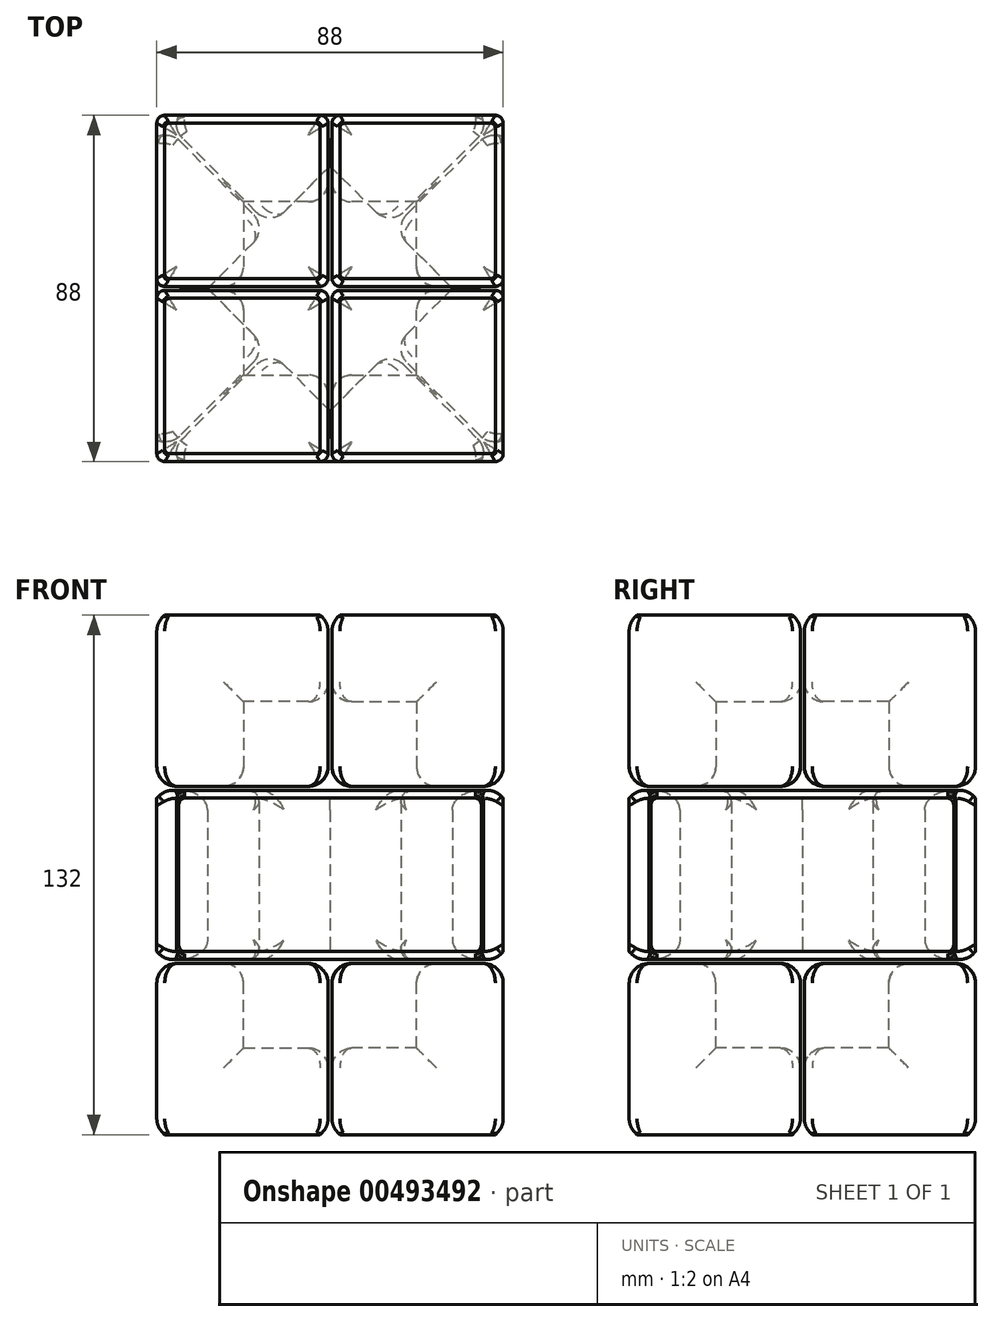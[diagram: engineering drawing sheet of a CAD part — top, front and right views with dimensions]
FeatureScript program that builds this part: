
annotation { "Feature Type Name" : "Feature", "Feature Type Description" : "" }
export const myFeature = defineFeature(function(context is Context, id is Id, definition is map)
    precondition{}
    {
        {
            assignVariable(context, id + "F0", {"name" : "Cubie", "anyValue" : 22});
        }
        {
            assignVariable(context, id + "F1", {"name" : "Tollerance", "anyValue" : 0.5});
        }
        {
            var Q0;
            Q0=qCreatedBy(makeId("Front.planeOp"),FACE);
            var sketch = newSketch(context, id + "F2", { "sketchPlane" : qUnion([Q0])});
            skLineSegment(sketch, "E0", {"start": v(0, 74.98) * mm, "end": v(0, -74.26) * mm, "construction": true});
            skSolve(sketch);
        }
        {
            var Q0;
            Q0=qCreatedBy(makeId("Top.planeOp"),FACE);
            var sketch = newSketch(context, id + "F3", { "sketchPlane" : qUnion([Q0])});
            skLineSegment(sketch, "E1.bottom", {"start": v(22, 22) * mm, "end": v(-22, 22) * mm});
            skLineSegment(sketch, "E1.top", {"start": v(22, -22) * mm, "end": v(-22, -22) * mm});
            skLineSegment(sketch, "E1.left", {"start": v(22, 22) * mm, "end": v(22, -22) * mm});
            skLineSegment(sketch, "E1.right", {"start": v(-22, 22) * mm, "end": v(-22, -22) * mm});
            skPoint(sketch, "E1.middle", {"position": v(0, 0) * mm});
            skLineSegment(sketch, "E2", {"start": v(0, 22) * mm, "end": v(0, -22) * mm});
            skLineSegment(sketch, "E3", {"start": v(-22, 0) * mm, "end": v(22, 0) * mm});
            skLineSegment(sketch, "E4", {"start": v(-31.11, 0) * mm, "end": v(0, 31.11) * mm});
            skLineSegment(sketch, "E5", {"start": v(0, 31.11) * mm, "end": v(31.11, 0) * mm});
            skLineSegment(sketch, "E6", {"start": v(31.11, 0) * mm, "end": v(0, -31.11) * mm});
            skLineSegment(sketch, "E7", {"start": v(0, -31.11) * mm, "end": v(-31.11, 0) * mm});
            skLineSegment(sketch, "E8", {"start": v(-15.56, 15.56) * mm, "end": v(15.56, -15.56) * mm});
            skLineSegment(sketch, "E9", {"start": v(-15.56, -15.56) * mm, "end": v(15.56, 15.56) * mm});
            skLineSegment(sketch, "E10.bottom", {"start": v(44, 44) * mm, "end": v(-44, 44) * mm});
            skLineSegment(sketch, "E10.top", {"start": v(44, -44) * mm, "end": v(-44, -44) * mm});
            skLineSegment(sketch, "E10.left", {"start": v(44, 44) * mm, "end": v(44, -44) * mm});
            skLineSegment(sketch, "E10.right", {"start": v(-44, 44) * mm, "end": v(-44, -44) * mm});
            skLineSegment(sketch, "E11", {"start": v(-44, 44) * mm, "end": v(44, -44) * mm});
            skLineSegment(sketch, "E12", {"start": v(-44, -44) * mm, "end": v(44, 44) * mm});
            skLineSegment(sketch, "E13", {"start": v(-44, 0) * mm, "end": v(44, 0) * mm});
            skLineSegment(sketch, "E14", {"start": v(0, 44) * mm, "end": v(0, -44) * mm});
            skLineSegment(sketch, "E15", {"start": v(-44, 44) * mm, "end": v(-22, 22) * mm});
            skLineSegment(sketch, "E16", {"start": v(22, 22) * mm, "end": v(44, 44) * mm});
            skSolve(sketch);
        }
        {
            var Q0;
            Q0=qCreatedBy(makeId("Top.planeOp"),FACE);
            var sketch = newSketch(context, id + "F4", { "sketchPlane" : qUnion([Q0])});
            skLineSegment(sketch, "E17", {"start": v(-15.2, 15.9) * mm, "end": v(-43.3, 44) * mm});
            skLineSegment(sketch, "E18", {"start": v(-43.3, 44) * mm, "end": v(43.3, 44) * mm});
            skLineSegment(sketch, "E19", {"start": v(43.3, 44) * mm, "end": v(15.2, 15.9) * mm});
            skLineSegment(sketch, "E20", {"start": v(15.2, 15.9) * mm, "end": v(0, 31.11) * mm});
            skLineSegment(sketch, "E21", {"start": v(0, 31.11) * mm, "end": v(-15.2, 15.9) * mm});
            skSolve(sketch);
        }
        {
            var Q0;
            Q0 = qSketchRegion(id + "F4", true);
            extrude(context, id + "F5", {"entities" : qUnion([Q0]), "endBound" : BoundingType.SYMMETRIC, "depth" : (getVariable(context, 'Cubie') * 2 - getVariable(context, 'Tollerance') * 2) * mm});
        }
        {
            var Q0;
            Q0=qCreatedBy(makeId("Top.planeOp"),FACE);
            var sketch = newSketch(context, id + "F6", { "sketchPlane" : qUnion([Q0])});
            skLineSegment(sketch, "E22", {"start": v(-44, 0.5) * mm, "end": v(-44, 44) * mm});
            skLineSegment(sketch, "E23", {"start": v(-44, 44) * mm, "end": v(-0.5, 44) * mm});
            skLineSegment(sketch, "E24", {"start": v(-0.5, 44) * mm, "end": v(-0.5, 22) * mm});
            skLineSegment(sketch, "E25", {"start": v(-0.5, 22) * mm, "end": v(-22, 22) * mm});
            skLineSegment(sketch, "E26", {"start": v(-22, 22) * mm, "end": v(-22, 0.5) * mm});
            skLineSegment(sketch, "E27", {"start": v(-22, 0.5) * mm, "end": v(-44, 0.5) * mm});
            skSolve(sketch);
        }
        {
            var Q0;
            Q0 = qSketchRegion(id + "F6", true);
            extrude(context, id + "F7", {"entities" : qUnion([Q0]), "depth" : (getVariable(context, 'Cubie') - getVariable(context, 'Tollerance')) * mm});
        }
        {
            var Q0;
            Q0=makeQuery(id+"F7.opExtrude","SWEPT_BODY",BODY,{"disambiguationData":[OSD([sQuery(id+"F6.wireOp",EDGE,"E22"),sQuery(id+"F6.wireOp",EDGE,"E23"),sQuery(id+"F6.wireOp",EDGE,"E24"),sQuery(id+"F6.wireOp",EDGE,"E25"),sQuery(id+"F6.wireOp",EDGE,"E26"),sQuery(id+"F6.wireOp",EDGE,"E27")])]});
            transform(context, id + "F8", {"entities" : qUnion([Q0]), "transformType" : TransformType.TRANSLATION_3D, "dx" : 0 * mm, "dy" : 0 * mm, "dz" : (getVariable(context, 'Cubie') + getVariable(context, 'Tollerance')) * mm, "makeCopy" : false});
        }
        {
            var Q0;
            Q0=makeQuery(id+"F7.opExtrude","CAP_FACE",FACE,{"disambiguationData":[OSD([sQuery(id+"F6.wireOp",EDGE,"E22"),sQuery(id+"F6.wireOp",EDGE,"E23"),sQuery(id+"F6.wireOp",EDGE,"E24"),sQuery(id+"F6.wireOp",EDGE,"E25"),sQuery(id+"F6.wireOp",EDGE,"E26"),sQuery(id+"F6.wireOp",EDGE,"E27")])],"isStart":false});
            var sketch = newSketch(context, id + "F9", { "sketchPlane" : qUnion([Q0])});
            skLineSegment(sketch, "E28", {"start": v(-44, 0.5) * mm, "end": v(-44, 44) * mm});
            skLineSegment(sketch, "E29", {"start": v(-44, 44) * mm, "end": v(-0.5, 44) * mm});
            skLineSegment(sketch, "E30", {"start": v(-0.5, 44) * mm, "end": v(-0.5, 0.5) * mm});
            skLineSegment(sketch, "E31", {"start": v(-0.5, 0.5) * mm, "end": v(-44, 0.5) * mm});
            skSolve(sketch);
        }
        {
            var Q0;
            Q0 = qSketchRegion(id + "F9", true);
            extrude(context, id + "F10", {"entities" : qUnion([Q0]), "operationType" : NewBodyOperationType.ADD, "depth" : (getVariable(context, 'Cubie')) * mm});
        }
        {
            var Q0;
            Q0=makeQuery(id+"F10.opExtrude","CAP_FACE",FACE,{"disambiguationData":[OSD([sQuery(id+"F9.wireOp",EDGE,"E28"),sQuery(id+"F9.wireOp",EDGE,"E29"),sQuery(id+"F9.wireOp",EDGE,"E30"),sQuery(id+"F9.wireOp",EDGE,"E31")])],"isStart":false});
            var Q1;
            Q1=makeQuery(id+"F5.opExtrude","SWEPT_FACE",FACE,{"disambiguationData":[OSD([sQuery(id+"F4.wireOp",EDGE,"E18")])]});
            chamfer(context, id + "F11", {"entities" : qUnion([Q0, Q1]), "width" : 2 * mm, "tangentPropagation" : true});
        }
        {
            var Q0;
            {var subQ0=sQuery(id+"F9.wireOp",EDGE,"E29");Q0=makeQuery(id+"F11.opChamfer","BLEND_EDGE",EDGE,{"blendedFrom":[makeQuery(id+"F10.opExtrude","CAP_EDGE",EDGE,{"disambiguationData":[OSD([subQ0])],"isStart":false}),makeQuery(id+"F10.boolean.opBoolean","MERGE",FACE,{"derivedFrom":[makeQuery(id+"F7.opExtrude","SWEPT_FACE",FACE,{"disambiguationData":[OSD([sQuery(id+"F6.wireOp",EDGE,"E23")])]}),makeQuery(id+"F10.opExtrude","SWEPT_FACE",FACE,{"disambiguationData":[OSD([subQ0])]})]})],"blendedInto":[makeQuery(id+"F10.boolean.opBoolean","MERGE",FACE,{"derivedFrom":[makeQuery(id+"F7.opExtrude","SWEPT_FACE",FACE,{"disambiguationData":[OSD([sQuery(id+"F6.wireOp",EDGE,"E23")])]}),makeQuery(id+"F10.opExtrude","SWEPT_FACE",FACE,{"disambiguationData":[OSD([subQ0])]})]})]});}
            var Q1;
            {var subQ0=sQuery(id+"F9.wireOp",EDGE,"E30");Q1=makeQuery(id+"F11.opChamfer","BLEND_EDGE",EDGE,{"blendedFrom":[makeQuery(id+"F10.opExtrude","CAP_EDGE",EDGE,{"disambiguationData":[OSD([subQ0])],"isStart":false}),makeQuery(id+"F10.boolean.opBoolean","MERGE",FACE,{"derivedFrom":[makeQuery(id+"F7.opExtrude","SWEPT_FACE",FACE,{"disambiguationData":[OSD([sQuery(id+"F6.wireOp",EDGE,"E24")])]}),makeQuery(id+"F10.opExtrude","SWEPT_FACE",FACE,{"disambiguationData":[OSD([subQ0])]})]})],"blendedInto":[makeQuery(id+"F10.boolean.opBoolean","MERGE",FACE,{"derivedFrom":[makeQuery(id+"F7.opExtrude","SWEPT_FACE",FACE,{"disambiguationData":[OSD([sQuery(id+"F6.wireOp",EDGE,"E24")])]}),makeQuery(id+"F10.opExtrude","SWEPT_FACE",FACE,{"disambiguationData":[OSD([subQ0])]})]})]});}
            var Q2;
            {var subQ0=sQuery(id+"F9.wireOp",EDGE,"E28");Q2=makeQuery(id+"F11.opChamfer","BLEND_EDGE",EDGE,{"blendedFrom":[makeQuery(id+"F10.opExtrude","CAP_EDGE",EDGE,{"disambiguationData":[OSD([subQ0])],"isStart":false}),makeQuery(id+"F10.boolean.opBoolean","MERGE",FACE,{"derivedFrom":[makeQuery(id+"F7.opExtrude","SWEPT_FACE",FACE,{"disambiguationData":[OSD([sQuery(id+"F6.wireOp",EDGE,"E22")])]}),makeQuery(id+"F10.opExtrude","SWEPT_FACE",FACE,{"disambiguationData":[OSD([subQ0])]})]})],"blendedInto":[makeQuery(id+"F10.boolean.opBoolean","MERGE",FACE,{"derivedFrom":[makeQuery(id+"F7.opExtrude","SWEPT_FACE",FACE,{"disambiguationData":[OSD([sQuery(id+"F6.wireOp",EDGE,"E22")])]}),makeQuery(id+"F10.opExtrude","SWEPT_FACE",FACE,{"disambiguationData":[OSD([subQ0])]})]})]});}
            var Q3;
            {var subQ0=sQuery(id+"F9.wireOp",EDGE,"E31");Q3=makeQuery(id+"F11.opChamfer","BLEND_EDGE",EDGE,{"blendedFrom":[makeQuery(id+"F10.opExtrude","CAP_EDGE",EDGE,{"disambiguationData":[OSD([subQ0])],"isStart":false}),makeQuery(id+"F10.boolean.opBoolean","MERGE",FACE,{"derivedFrom":[makeQuery(id+"F7.opExtrude","SWEPT_FACE",FACE,{"disambiguationData":[OSD([sQuery(id+"F6.wireOp",EDGE,"E27")])]}),makeQuery(id+"F10.opExtrude","SWEPT_FACE",FACE,{"disambiguationData":[OSD([subQ0])]})]})],"blendedInto":[makeQuery(id+"F10.boolean.opBoolean","MERGE",FACE,{"derivedFrom":[makeQuery(id+"F7.opExtrude","SWEPT_FACE",FACE,{"disambiguationData":[OSD([sQuery(id+"F6.wireOp",EDGE,"E27")])]}),makeQuery(id+"F10.opExtrude","SWEPT_FACE",FACE,{"disambiguationData":[OSD([subQ0])]})]})]});}
            var Q4;
            Q4=makeQuery(id+"F7.opExtrude","CAP_FACE",FACE,{"disambiguationData":[OSD([sQuery(id+"F6.wireOp",EDGE,"E22"),sQuery(id+"F6.wireOp",EDGE,"E23"),sQuery(id+"F6.wireOp",EDGE,"E24"),sQuery(id+"F6.wireOp",EDGE,"E25"),sQuery(id+"F6.wireOp",EDGE,"E26"),sQuery(id+"F6.wireOp",EDGE,"E27")])],"isStart":true});
            var Q5;
            Q5=makeQuery(id+"F7.opExtrude","SWEPT_EDGE",EDGE,{"disambiguationData":[OSD([sQuery(id+"F6.wireOp",EDGE,"E26"),sQuery(id+"F6.wireOp",EDGE,"E27")])]});
            var Q6;
            Q6=makeQuery(id+"F10.opExtrude","CAP_EDGE",EDGE,{"disambiguationData":[OSD([sQuery(id+"F9.wireOp",EDGE,"E31")])],"isStart":true});
            var Q7;
            Q7=makeQuery(id+"F10.opExtrude","CAP_EDGE",EDGE,{"disambiguationData":[OSD([sQuery(id+"F9.wireOp",EDGE,"E30")])],"isStart":true});
            var Q8;
            Q8=makeQuery(id+"F7.opExtrude","SWEPT_EDGE",EDGE,{"disambiguationData":[OSD([sQuery(id+"F6.wireOp",EDGE,"E24"),sQuery(id+"F6.wireOp",EDGE,"E25")])]});
            var Q9;
            {var subQ0=sQuery(id+"F4.wireOp",EDGE,"E17");Q9=makeQuery(id+"F11.opChamfer","BLEND_EDGE",EDGE,{"blendedFrom":[makeQuery(id+"F5.opExtrude","SWEPT_EDGE",EDGE,{"disambiguationData":[OSD([subQ0,sQuery(id+"F4.wireOp",EDGE,"E18")])]}),makeQuery(id+"F5.opExtrude","SWEPT_FACE",FACE,{"disambiguationData":[OSD([subQ0])]})],"blendedInto":[makeQuery(id+"F5.opExtrude","SWEPT_FACE",FACE,{"disambiguationData":[OSD([subQ0])]})]});}
            var Q10;
            {var subQ0=sQuery(id+"F4.wireOp",EDGE,"E18");Q10=makeQuery(id+"F11.opChamfer","BLEND_EDGE",EDGE,{"blendedFrom":[makeQuery(id+"F5.opExtrude","CAP_EDGE",EDGE,{"disambiguationData":[OSD([subQ0])],"isStart":true}),makeQuery(id+"F5.opExtrude","CAP_FACE",FACE,{"disambiguationData":[OSD([sQuery(id+"F4.wireOp",EDGE,"E17"),subQ0,sQuery(id+"F4.wireOp",EDGE,"E19"),sQuery(id+"F4.wireOp",EDGE,"E20"),sQuery(id+"F4.wireOp",EDGE,"E21")])],"isStart":true})],"blendedInto":[makeQuery(id+"F5.opExtrude","CAP_FACE",FACE,{"disambiguationData":[OSD([sQuery(id+"F4.wireOp",EDGE,"E17"),subQ0,sQuery(id+"F4.wireOp",EDGE,"E19"),sQuery(id+"F4.wireOp",EDGE,"E20"),sQuery(id+"F4.wireOp",EDGE,"E21")])],"isStart":true})]});}
            var Q11;
            {var subQ0=sQuery(id+"F4.wireOp",EDGE,"E19");Q11=makeQuery(id+"F11.opChamfer","BLEND_EDGE",EDGE,{"blendedFrom":[makeQuery(id+"F5.opExtrude","SWEPT_EDGE",EDGE,{"disambiguationData":[OSD([sQuery(id+"F4.wireOp",EDGE,"E18"),subQ0])]}),makeQuery(id+"F5.opExtrude","SWEPT_FACE",FACE,{"disambiguationData":[OSD([subQ0])]})],"blendedInto":[makeQuery(id+"F5.opExtrude","SWEPT_FACE",FACE,{"disambiguationData":[OSD([subQ0])]})]});}
            var Q12;
            {var subQ0=sQuery(id+"F4.wireOp",EDGE,"E18");Q12=makeQuery(id+"F11.opChamfer","BLEND_EDGE",EDGE,{"blendedFrom":[makeQuery(id+"F5.opExtrude","CAP_EDGE",EDGE,{"disambiguationData":[OSD([subQ0])],"isStart":false}),makeQuery(id+"F5.opExtrude","CAP_FACE",FACE,{"disambiguationData":[OSD([sQuery(id+"F4.wireOp",EDGE,"E17"),subQ0,sQuery(id+"F4.wireOp",EDGE,"E19"),sQuery(id+"F4.wireOp",EDGE,"E20"),sQuery(id+"F4.wireOp",EDGE,"E21")])],"isStart":false})],"blendedInto":[makeQuery(id+"F5.opExtrude","CAP_FACE",FACE,{"disambiguationData":[OSD([sQuery(id+"F4.wireOp",EDGE,"E17"),subQ0,sQuery(id+"F4.wireOp",EDGE,"E19"),sQuery(id+"F4.wireOp",EDGE,"E20"),sQuery(id+"F4.wireOp",EDGE,"E21")])],"isStart":false})]});}
            var Q13;
            Q13=makeQuery(id+"F5.opExtrude","SWEPT_EDGE",EDGE,{"disambiguationData":[OSD([sQuery(id+"F4.wireOp",EDGE,"E17"),sQuery(id+"F4.wireOp",EDGE,"E21")])]});
            var Q14;
            Q14=makeQuery(id+"F5.opExtrude","SWEPT_EDGE",EDGE,{"disambiguationData":[OSD([sQuery(id+"F4.wireOp",EDGE,"E19"),sQuery(id+"F4.wireOp",EDGE,"E20")])]});
            var Q15;
            Q15=makeQuery(id+"F5.opExtrude","CAP_EDGE",EDGE,{"disambiguationData":[OSD([sQuery(id+"F4.wireOp",EDGE,"E20")])],"isStart":false});
            var Q16;
            Q16=makeQuery(id+"F5.opExtrude","CAP_EDGE",EDGE,{"disambiguationData":[OSD([sQuery(id+"F4.wireOp",EDGE,"E21")])],"isStart":false});
            var Q17;
            Q17=makeQuery(id+"F5.opExtrude","CAP_EDGE",EDGE,{"disambiguationData":[OSD([sQuery(id+"F4.wireOp",EDGE,"E20")])],"isStart":true});
            var Q18;
            Q18=makeQuery(id+"F5.opExtrude","CAP_EDGE",EDGE,{"disambiguationData":[OSD([sQuery(id+"F4.wireOp",EDGE,"E21")])],"isStart":true});
            fillet(context, id + "F12", {"entities" : qUnion([Q0, Q1, Q2, Q3, Q4, Q5, Q6, Q7, Q8, Q9, Q10, Q11, Q12, Q13, Q14, Q15, Q16, Q17, Q18]), "radius" : 5 * mm, "tangentPropagation" : true, "allowEdgeOverflow" : false});
        }
        {
            var Q0;
            Q0=makeQuery(id+"F5.opExtrude","CAP_EDGE",EDGE,{"disambiguationData":[OSD([sQuery(id+"F4.wireOp",EDGE,"E17")])],"isStart":true});
            var Q1;
            Q1=makeQuery(id+"F5.opExtrude","CAP_EDGE",EDGE,{"disambiguationData":[OSD([sQuery(id+"F4.wireOp",EDGE,"E17")])],"isStart":false});
            var Q2;
            Q2=makeQuery(id+"F5.opExtrude","CAP_EDGE",EDGE,{"disambiguationData":[OSD([sQuery(id+"F4.wireOp",EDGE,"E19")])],"isStart":true});
            var Q3;
            Q3=makeQuery(id+"F5.opExtrude","CAP_EDGE",EDGE,{"disambiguationData":[OSD([sQuery(id+"F4.wireOp",EDGE,"E19")])],"isStart":false});
            var Q4;
            Q4=makeQuery(id+"F10.boolean.opBoolean","MERGE",EDGE,{"derivedFrom":[makeQuery(id+"F7.opExtrude","SWEPT_EDGE",EDGE,{"disambiguationData":[OSD([sQuery(id+"F6.wireOp",EDGE,"E22"),sQuery(id+"F6.wireOp",EDGE,"E27")])]}),makeQuery(id+"F10.opExtrude","SWEPT_EDGE",EDGE,{"disambiguationData":[OSD([sQuery(id+"F9.wireOp",EDGE,"E28"),sQuery(id+"F9.wireOp",EDGE,"E31")])]})]});
            var Q5;
            Q5=makeQuery(id+"F10.boolean.opBoolean","MERGE",EDGE,{"derivedFrom":[makeQuery(id+"F7.opExtrude","SWEPT_EDGE",EDGE,{"disambiguationData":[OSD([sQuery(id+"F6.wireOp",EDGE,"E22"),sQuery(id+"F6.wireOp",EDGE,"E23")])]}),makeQuery(id+"F10.opExtrude","SWEPT_EDGE",EDGE,{"disambiguationData":[OSD([sQuery(id+"F9.wireOp",EDGE,"E28"),sQuery(id+"F9.wireOp",EDGE,"E29")])]})]});
            var Q6;
            Q6=makeQuery(id+"F10.boolean.opBoolean","MERGE",EDGE,{"derivedFrom":[makeQuery(id+"F7.opExtrude","SWEPT_EDGE",EDGE,{"disambiguationData":[OSD([sQuery(id+"F6.wireOp",EDGE,"E23"),sQuery(id+"F6.wireOp",EDGE,"E24")])]}),makeQuery(id+"F10.opExtrude","SWEPT_EDGE",EDGE,{"disambiguationData":[OSD([sQuery(id+"F9.wireOp",EDGE,"E29"),sQuery(id+"F9.wireOp",EDGE,"E30")])]})]});
            var Q7;
            Q7=makeQuery(id+"F10.opExtrude","SWEPT_EDGE",EDGE,{"disambiguationData":[OSD([sQuery(id+"F9.wireOp",EDGE,"E30"),sQuery(id+"F9.wireOp",EDGE,"E31")])]});
            fillet(context, id + "F13", {"entities" : qUnion([Q0, Q1, Q2, Q3, Q4, Q5, Q6, Q7]), "radius" : 2 * mm, "tangentPropagation" : true, "allowEdgeOverflow" : false});
        }
        {
            var Q0;
            Q0=makeQuery(id+"F7.opExtrude","SWEPT_BODY",BODY,{"disambiguationData":[OSD([sQuery(id+"F6.wireOp",EDGE,"E22"),sQuery(id+"F6.wireOp",EDGE,"E23"),sQuery(id+"F6.wireOp",EDGE,"E24"),sQuery(id+"F6.wireOp",EDGE,"E25"),sQuery(id+"F6.wireOp",EDGE,"E26"),sQuery(id+"F6.wireOp",EDGE,"E27")])]});
            var Q1;
            Q1=makeQuery(id+"F5.opExtrude","SWEPT_BODY",BODY,{"disambiguationData":[OSD([sQuery(id+"F4.wireOp",EDGE,"E17"),sQuery(id+"F4.wireOp",EDGE,"E18"),sQuery(id+"F4.wireOp",EDGE,"E19"),sQuery(id+"F4.wireOp",EDGE,"E20"),sQuery(id+"F4.wireOp",EDGE,"E21")])]});
            var Q2;
            Q2=sQuery(id+"F2.wireOp",EDGE,"E0");
            circularPattern(context, id + "F14", {"entities" : qUnion([Q0, Q1]), "axis" : qUnion([Q2]), "angle" : 360 * degree, "instanceCount" : 4, "equalSpace" : true});
        }
        {
            var Q0;
            Q0=makeQuery(id+"F14.opPattern","COPY",BODY,{"derivedFrom":makeQuery(id+"F7.opExtrude","SWEPT_BODY",BODY,{"disambiguationData":[OSD([sQuery(id+"F6.wireOp",EDGE,"E22"),sQuery(id+"F6.wireOp",EDGE,"E23"),sQuery(id+"F6.wireOp",EDGE,"E24"),sQuery(id+"F6.wireOp",EDGE,"E25"),sQuery(id+"F6.wireOp",EDGE,"E26"),sQuery(id+"F6.wireOp",EDGE,"E27")])]}),"instanceName":"3"});
            var Q1;
            Q1=makeQuery(id+"F7.opExtrude","SWEPT_BODY",BODY,{"disambiguationData":[OSD([sQuery(id+"F6.wireOp",EDGE,"E22"),sQuery(id+"F6.wireOp",EDGE,"E23"),sQuery(id+"F6.wireOp",EDGE,"E24"),sQuery(id+"F6.wireOp",EDGE,"E25"),sQuery(id+"F6.wireOp",EDGE,"E26"),sQuery(id+"F6.wireOp",EDGE,"E27")])]});
            var Q2;
            Q2=makeQuery(id+"F14.opPattern","COPY",BODY,{"derivedFrom":makeQuery(id+"F7.opExtrude","SWEPT_BODY",BODY,{"disambiguationData":[OSD([sQuery(id+"F6.wireOp",EDGE,"E22"),sQuery(id+"F6.wireOp",EDGE,"E23"),sQuery(id+"F6.wireOp",EDGE,"E24"),sQuery(id+"F6.wireOp",EDGE,"E25"),sQuery(id+"F6.wireOp",EDGE,"E26"),sQuery(id+"F6.wireOp",EDGE,"E27")])]}),"instanceName":"1"});
            var Q3;
            Q3=makeQuery(id+"F14.opPattern","COPY",BODY,{"derivedFrom":makeQuery(id+"F7.opExtrude","SWEPT_BODY",BODY,{"disambiguationData":[OSD([sQuery(id+"F6.wireOp",EDGE,"E22"),sQuery(id+"F6.wireOp",EDGE,"E23"),sQuery(id+"F6.wireOp",EDGE,"E24"),sQuery(id+"F6.wireOp",EDGE,"E25"),sQuery(id+"F6.wireOp",EDGE,"E26"),sQuery(id+"F6.wireOp",EDGE,"E27")])]}),"instanceName":"2"});
            var Q4;
            Q4=qCreatedBy(makeId("Top.planeOp"),FACE);
            mirror(context, id + "F15", {"entities" : qUnion([Q0, Q1, Q2, Q3]), "mirrorPlane" : qUnion([Q4])});
        }
    });
